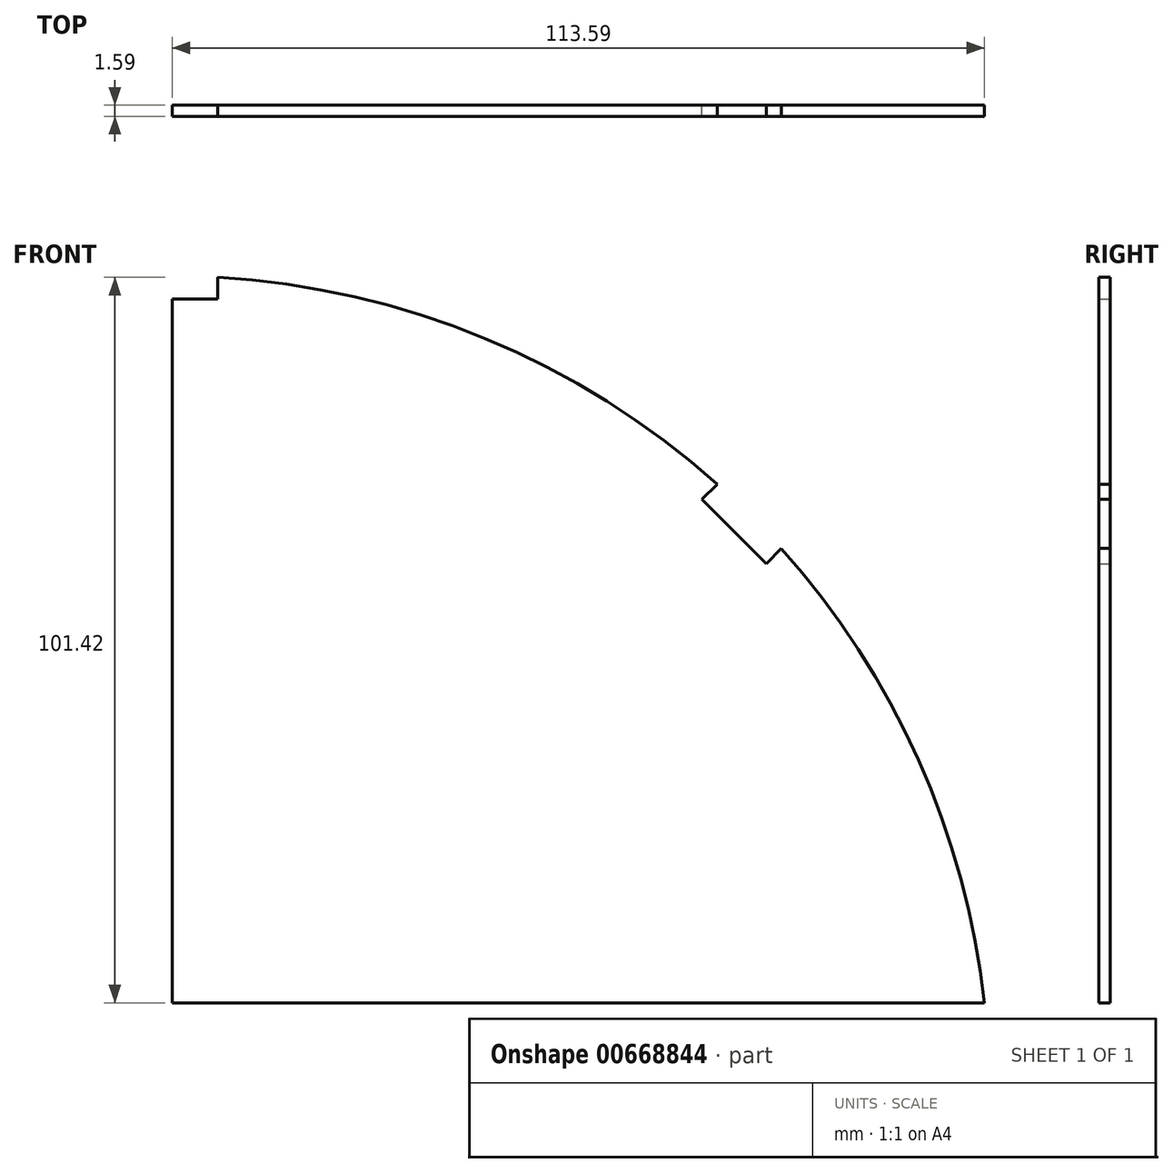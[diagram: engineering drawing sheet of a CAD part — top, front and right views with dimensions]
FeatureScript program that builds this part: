
annotation { "Feature Type Name" : "Feature", "Feature Type Description" : "" }
export const myFeature = defineFeature(function(context is Context, id is Id, definition is map)
    precondition{}
    {
        {
            var Q0;
            Q0=qCreatedBy(makeId("Front.planeOp"),FACE);
            var sketch = newSketch(context, id + "F0", { "sketchPlane" : qUnion([Q0])});
            skCircle(sketch, "E0", {"center": v(0, 0) * mm, "radius": 114.3 * mm});
            skLineSegment(sketch, "E1", {"start": v(0, 114.3) * mm, "end": v(0, -116.9) * mm, "construction": true});
            skLineSegment(sketch, "E2", {"start": v(-114.3, 0) * mm, "end": v(114.3, 0) * mm, "construction": true});
            skLineSegment(sketch, "E3", {"start": v(0, 0) * mm, "end": v(80.82, 80.82) * mm, "construction": true});
            skLineSegment(sketch, "E4", {"start": v(80.82, 80.82) * mm, "end": v(0, 0) * mm, "construction": true});
            skLineSegment(sketch, "E5", {"start": v(0, 0) * mm, "end": v(-80.82, 80.82) * mm, "construction": true});
            skLineSegment(sketch, "E6", {"start": v(0, 111.13) * mm, "end": v(6.35, 111.13) * mm});
            skLineSegment(sketch, "E7", {"start": v(6.35, 111.13) * mm, "end": v(6.35, 114.12) * mm});
            skLineSegment(sketch, "E8.MirrorCS", {"start": v(0, 111.13) * mm, "end": v(-6.35, 111.13) * mm});
            skLineSegment(sketch, "E9", {"start": v(-6.35, 111.13) * mm, "end": v(-6.35, 114.12) * mm});
            skLineSegment(sketch, "E10", {"start": v(78.58, 78.58) * mm, "end": v(83.07, 74.09) * mm});
            skLineSegment(sketch, "E11", {"start": v(83.07, 74.09) * mm, "end": v(85.19, 76.2) * mm});
            skLineSegment(sketch, "E12.MirrorCS", {"start": v(78.58, 78.58) * mm, "end": v(74.09, 83.07) * mm});
            skLineSegment(sketch, "E13", {"start": v(74.09, 83.07) * mm, "end": v(76.33, 85.31) * mm});
            skLineSegment(sketch, "E14", {"start": v(-78.58, 78.58) * mm, "end": v(-74.09, 83.07) * mm});
            skLineSegment(sketch, "E15", {"start": v(-74.09, 83.07) * mm, "end": v(-76.2, 85.19) * mm});
            skLineSegment(sketch, "E16.MirrorCS", {"start": v(-78.58, 78.58) * mm, "end": v(-83.07, 74.09) * mm});
            skLineSegment(sketch, "E17", {"start": v(-83.07, 74.09) * mm, "end": v(-85.19, 76.2) * mm});
            skLineSegment(sketch, "E18", {"start": v(-114.3, 0) * mm, "end": v(114.3, 0) * mm});
            skLineSegment(sketch, "E19", {"start": v(-113.6, 12.7) * mm, "end": v(113.6, 12.7) * mm});
            skLineSegment(sketch, "E20", {"start": v(0, 0) * mm, "end": v(0, 111.13) * mm});
            skLineSegment(sketch, "E21", {"start": v(0, 0) * mm, "end": v(-75.31, 75.31) * mm});
            skSolve(sketch);
        }
        {
            var Q0;
            Q0=makeQuery(id+"F0.imprint","IMPRINT",FACE,{"disambiguationData":[TD([[makeQuery(id+"F0.imprint","IMPRINT",EDGE,{"derivedFrom":sQuery(id+"F0.wireOp",EDGE,"E6")}),-1.0]])]});
            extrude(context, id + "F1", {"entities" : qUnion([Q0]), "depth" : 1.59 * mm, "offsetDistance" : 25.4 * mm});
        }
    });
